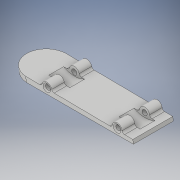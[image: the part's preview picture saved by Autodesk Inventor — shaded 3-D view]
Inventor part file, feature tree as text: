
AUTODESK INVENTOR PART (.ipt)
format: ipt  version: 2018.3 (Build 223284000, 284)  size: 171,008 bytes
history: native  units: in
note: dims shown in document units (in); Inventor stores cm internally (conversion verified against a paired STEP export)
features: extrude x3, sketch x2, plane x1, chamfer x1
ambient origin geometry x8: Origin, YZ Plane, XZ Plane, XY Plane, X Axis, Y Axis, Z Axis, Center Point
bodies: Body1 (feature_tree)
feature tree (7):
  sketch  "Sketch2"  dims[d5=0.6803in d6=0.046in]
  extrude  "Extrusion2"  Depth=0.046in
  plane  "Work Plane1"
  extrude  "Extrusion3"  Depth=0.18in
  extrude  "Extrusion4"  Depth=0.18in
  chamfer  "Chamfer1"  Distance=0.063in
  sketch  "Sketch4"  dims[d7=0.063in d9=0.063in d10=0.183in d11=0.063in d12=0.854in d13=1.51in d14=0.068in d15=0.12in d16=0.12in d17=0.03in d18=0.485in d19=0.0in d20=0.486in d21=0.485in d22=0.0in d23=0.54in d24=0.54in d25=0.18in d26=0.0in d27=0.015in d28=0.125in d29=45.0deg]
